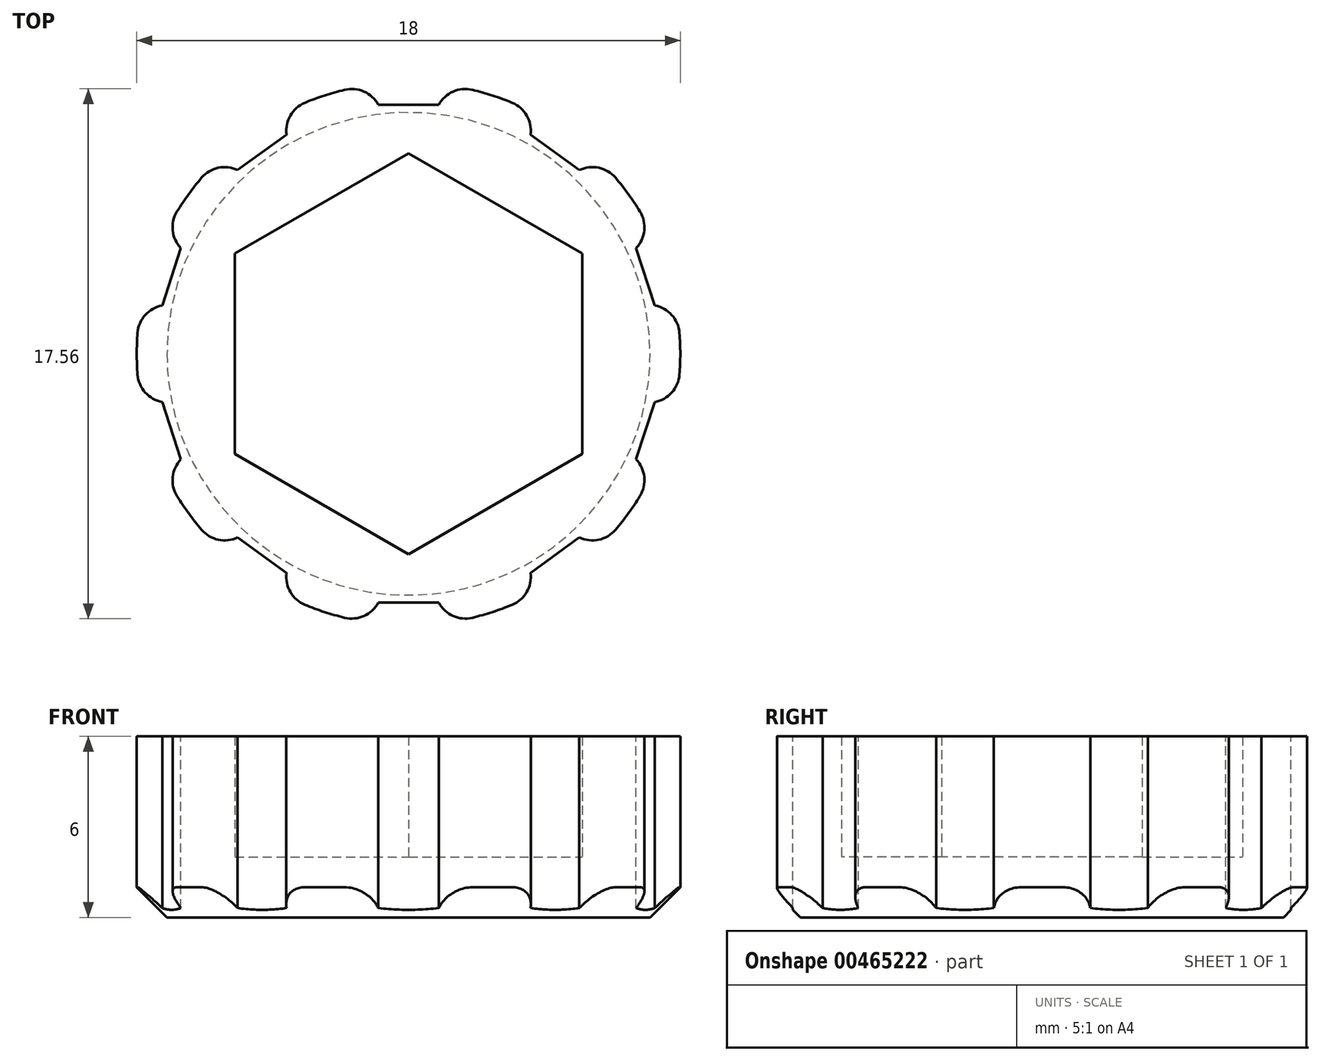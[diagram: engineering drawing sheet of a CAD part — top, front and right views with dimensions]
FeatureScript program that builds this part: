
annotation { "Feature Type Name" : "Feature", "Feature Type Description" : "" }
export const myFeature = defineFeature(function(context is Context, id is Id, definition is map)
    precondition{}
    {
        {
            var Q0;
            Q0=qCreatedBy(makeId("Top.planeOp"),FACE);
            var sketch = newSketch(context, id + "F0", { "sketchPlane" : qUnion([Q0])});
            skCircle(sketch, "E0.cCircle", {"center": v(0, 0) * mm, "radius": 5.75 * mm, "construction": true});
            skLineSegment(sketch, "E0.0", {"start": v(0, 6.64) * mm, "end": v(5.75, 3.32) * mm});
            skLineSegment(sketch, "E0.1", {"start": v(5.75, 3.32) * mm, "end": v(5.75, -3.32) * mm});
            skLineSegment(sketch, "E0.2", {"start": v(5.75, -3.32) * mm, "end": v(0, -6.64) * mm});
            skLineSegment(sketch, "E0.3", {"start": v(0, -6.64) * mm, "end": v(-5.75, -3.32) * mm});
            skLineSegment(sketch, "E0.4", {"start": v(-5.75, -3.32) * mm, "end": v(-5.75, 3.32) * mm});
            skLineSegment(sketch, "E0.5", {"start": v(-5.75, 3.32) * mm, "end": v(0, 6.64) * mm});
            skPoint(sketch, "E0.0.midPoint", {"position": v(2.87, 4.98) * mm});
            skCircle(sketch, "E1", {"center": v(0, 0) * mm, "radius": 9 * mm});
            skSolve(sketch);
        }
        {
            var Q0;
            Q0 = qSketchRegion(id + "F0", true);
            extrude(context, id + "F1", {"entities" : qUnion([Q0]), "depth" : 4 * mm});
        }
        {
            var Q0;
            Q0=makeQuery(id+"F1.opExtrude","CAP_FACE",FACE,{"disambiguationData":[OSD([sQuery(id+"F0.wireOp",EDGE,"E0.0"),sQuery(id+"F0.wireOp",EDGE,"E0.1"),sQuery(id+"F0.wireOp",EDGE,"E0.2"),sQuery(id+"F0.wireOp",EDGE,"E0.3"),sQuery(id+"F0.wireOp",EDGE,"E0.4"),sQuery(id+"F0.wireOp",EDGE,"E0.5"),sQuery(id+"F0.wireOp",EDGE,"E1")])],"isStart":true});
            var sketch = newSketch(context, id + "F2", { "sketchPlane" : qUnion([Q0])});
            skCircle(sketch, "E2.0", {"center": v(0, 0) * mm, "radius": 9 * mm});
            skSolve(sketch);
        }
        {
            var Q0;
            Q0 = qSketchRegion(id + "F2", true);
            extrude(context, id + "F3", {"entities" : qUnion([Q0]), "operationType" : NewBodyOperationType.ADD, "depth" : 2 * mm});
        }
        {
            var Q0;
            Q0=makeQuery(id+"F3.opExtrude","CAP_EDGE",EDGE,{"disambiguationData":[OSD([sQuery(id+"F2.wireOp",EDGE,"E2.0")])],"isStart":false});
            chamfer(context, id + "F4", {"entities" : qUnion([Q0]), "width" : 1 * mm, "tangentPropagation" : true});
        }
        {
            var Q0;
            Q0=makeQuery(id+"F1.opExtrude","CAP_FACE",FACE,{"disambiguationData":[OSD([sQuery(id+"F0.wireOp",EDGE,"E0.0"),sQuery(id+"F0.wireOp",EDGE,"E0.1"),sQuery(id+"F0.wireOp",EDGE,"E0.2"),sQuery(id+"F0.wireOp",EDGE,"E0.3"),sQuery(id+"F0.wireOp",EDGE,"E0.4"),sQuery(id+"F0.wireOp",EDGE,"E0.5"),sQuery(id+"F0.wireOp",EDGE,"E1")])],"isStart":false});
            var sketch = newSketch(context, id + "F5", { "sketchPlane" : qUnion([Q0])});
            skLineSegment(sketch, "E3.bottom", {"start": v(1, 9.75) * mm, "end": v(-1, 9.75) * mm});
            skLineSegment(sketch, "E3.top", {"start": v(1, 8.25) * mm, "end": v(-1, 8.25) * mm});
            skLineSegment(sketch, "E3.left", {"start": v(1, 9.75) * mm, "end": v(1, 8.25) * mm});
            skLineSegment(sketch, "E3.right", {"start": v(-1, 9.75) * mm, "end": v(-1, 8.25) * mm});
            skPoint(sketch, "E3.middle", {"position": v(0, 9) * mm});
            skLineSegment(sketch, "E4.1.0", {"start": v(-4.92, 8.48) * mm, "end": v(-6.54, 7.3) * mm});
            skLineSegment(sketch, "E4.1.1", {"start": v(-6.54, 7.3) * mm, "end": v(-5.66, 6.09) * mm});
            skLineSegment(sketch, "E4.1.2", {"start": v(-4.04, 7.26) * mm, "end": v(-5.66, 6.09) * mm});
            skLineSegment(sketch, "E4.1.3", {"start": v(-4.92, 8.48) * mm, "end": v(-4.04, 7.26) * mm});
            skLineSegment(sketch, "E4.2.0", {"start": v(-8.96, 3.96) * mm, "end": v(-9.58, 2.06) * mm});
            skLineSegment(sketch, "E4.2.1", {"start": v(-9.58, 2.06) * mm, "end": v(-8.16, 1.6) * mm});
            skLineSegment(sketch, "E4.2.2", {"start": v(-7.54, 3.5) * mm, "end": v(-8.16, 1.6) * mm});
            skLineSegment(sketch, "E4.2.3", {"start": v(-8.96, 3.96) * mm, "end": v(-7.54, 3.5) * mm});
            skPoint(sketch, "E4.center", {"position": v(0, 0) * mm});
            skLineSegment(sketch, "E5.2.3.0", {"start": v(-9.58, -2.06) * mm, "end": v(-8.96, -3.96) * mm});
            skLineSegment(sketch, "E5.3.3.0", {"start": v(-8.96, -3.96) * mm, "end": v(-7.54, -3.5) * mm});
            skLineSegment(sketch, "E5.6.3.0", {"start": v(-8.16, -1.6) * mm, "end": v(-7.54, -3.5) * mm});
            skLineSegment(sketch, "E5.9.3.0", {"start": v(-9.58, -2.06) * mm, "end": v(-8.16, -1.6) * mm});
            skLineSegment(sketch, "E5.2.4.0", {"start": v(-6.54, -7.3) * mm, "end": v(-4.92, -8.48) * mm});
            skLineSegment(sketch, "E5.3.4.0", {"start": v(-4.92, -8.48) * mm, "end": v(-4.04, -7.26) * mm});
            skLineSegment(sketch, "E5.6.4.0", {"start": v(-5.66, -6.09) * mm, "end": v(-4.04, -7.26) * mm});
            skLineSegment(sketch, "E5.9.4.0", {"start": v(-6.54, -7.3) * mm, "end": v(-5.66, -6.09) * mm});
            skLineSegment(sketch, "E5.2.5.0", {"start": v(-1, -9.75) * mm, "end": v(1, -9.75) * mm});
            skLineSegment(sketch, "E5.3.5.0", {"start": v(1, -9.75) * mm, "end": v(1, -8.25) * mm});
            skLineSegment(sketch, "E5.6.5.0", {"start": v(-1, -8.25) * mm, "end": v(1, -8.25) * mm});
            skLineSegment(sketch, "E5.9.5.0", {"start": v(-1, -9.75) * mm, "end": v(-1, -8.25) * mm});
            skLineSegment(sketch, "E5.2.6.0", {"start": v(4.92, -8.48) * mm, "end": v(6.54, -7.3) * mm});
            skLineSegment(sketch, "E5.3.6.0", {"start": v(6.54, -7.3) * mm, "end": v(5.66, -6.09) * mm});
            skLineSegment(sketch, "E5.6.6.0", {"start": v(4.04, -7.26) * mm, "end": v(5.66, -6.09) * mm});
            skLineSegment(sketch, "E5.9.6.0", {"start": v(4.92, -8.48) * mm, "end": v(4.04, -7.26) * mm});
            skLineSegment(sketch, "E5.2.7.0", {"start": v(8.96, -3.96) * mm, "end": v(9.58, -2.06) * mm});
            skLineSegment(sketch, "E5.3.7.0", {"start": v(9.58, -2.06) * mm, "end": v(8.16, -1.6) * mm});
            skLineSegment(sketch, "E5.6.7.0", {"start": v(7.54, -3.5) * mm, "end": v(8.16, -1.6) * mm});
            skLineSegment(sketch, "E5.9.7.0", {"start": v(8.96, -3.96) * mm, "end": v(7.54, -3.5) * mm});
            skLineSegment(sketch, "E5.2.8.0", {"start": v(9.58, 2.06) * mm, "end": v(8.96, 3.96) * mm});
            skLineSegment(sketch, "E5.3.8.0", {"start": v(8.96, 3.96) * mm, "end": v(7.54, 3.5) * mm});
            skLineSegment(sketch, "E5.6.8.0", {"start": v(8.16, 1.6) * mm, "end": v(7.54, 3.5) * mm});
            skLineSegment(sketch, "E5.9.8.0", {"start": v(9.58, 2.06) * mm, "end": v(8.16, 1.6) * mm});
            skLineSegment(sketch, "E5.2.9.0", {"start": v(6.54, 7.3) * mm, "end": v(4.92, 8.48) * mm});
            skLineSegment(sketch, "E5.3.9.0", {"start": v(4.92, 8.48) * mm, "end": v(4.04, 7.26) * mm});
            skLineSegment(sketch, "E5.6.9.0", {"start": v(5.66, 6.09) * mm, "end": v(4.04, 7.26) * mm});
            skLineSegment(sketch, "E5.9.9.0", {"start": v(6.54, 7.3) * mm, "end": v(5.66, 6.09) * mm});
            skSolve(sketch);
        }
        {
            var Q0;
            Q0 = qSketchRegion(id + "F5", true);
            extrude(context, id + "F6", {"entities" : qUnion([Q0]), "operationType" : NewBodyOperationType.REMOVE, "endBound" : BoundingType.THROUGH_ALL, "oppositeDirection" : true, "depth" : 25 * mm});
        }
        {
            var Q0;
            Q0=makeQuery(id+"F6.boolean.opBoolean","INTERSECT",EDGE,{"derivedFrom":[makeQuery(id+"F3.boolean.opBoolean","MERGE",FACE,{"derivedFrom":[makeQuery(id+"F1.opExtrude","SWEPT_FACE",FACE,{"disambiguationData":[OSD([sQuery(id+"F0.wireOp",EDGE,"E1")])]}),makeQuery(id+"F3.opExtrude","SWEPT_FACE",FACE,{"disambiguationData":[OSD([sQuery(id+"F2.wireOp",EDGE,"E2.0")])]})]}),makeQuery(id+"F6.opExtrude","SWEPT_FACE",FACE,{"disambiguationData":[OSD([sQuery(id+"F5.wireOp",EDGE,"E3.left")])]})]});
            var Q1;
            Q1=makeQuery(id+"F6.boolean.opBoolean","INTERSECT",EDGE,{"derivedFrom":[makeQuery(id+"F3.boolean.opBoolean","MERGE",FACE,{"derivedFrom":[makeQuery(id+"F1.opExtrude","SWEPT_FACE",FACE,{"disambiguationData":[OSD([sQuery(id+"F0.wireOp",EDGE,"E1")])]}),makeQuery(id+"F3.opExtrude","SWEPT_FACE",FACE,{"disambiguationData":[OSD([sQuery(id+"F2.wireOp",EDGE,"E2.0")])]})]}),makeQuery(id+"F6.opExtrude","SWEPT_FACE",FACE,{"disambiguationData":[OSD([sQuery(id+"F5.wireOp",EDGE,"E5.3.9.0")])]})]});
            var Q2;
            Q2=makeQuery(id+"F6.boolean.opBoolean","INTERSECT",EDGE,{"derivedFrom":[makeQuery(id+"F3.boolean.opBoolean","MERGE",FACE,{"derivedFrom":[makeQuery(id+"F1.opExtrude","SWEPT_FACE",FACE,{"disambiguationData":[OSD([sQuery(id+"F0.wireOp",EDGE,"E1")])]}),makeQuery(id+"F3.opExtrude","SWEPT_FACE",FACE,{"disambiguationData":[OSD([sQuery(id+"F2.wireOp",EDGE,"E2.0")])]})]}),makeQuery(id+"F6.opExtrude","SWEPT_FACE",FACE,{"disambiguationData":[OSD([sQuery(id+"F5.wireOp",EDGE,"E5.9.9.0")])]})]});
            var Q3;
            Q3=makeQuery(id+"F6.boolean.opBoolean","INTERSECT",EDGE,{"derivedFrom":[makeQuery(id+"F3.boolean.opBoolean","MERGE",FACE,{"derivedFrom":[makeQuery(id+"F1.opExtrude","SWEPT_FACE",FACE,{"disambiguationData":[OSD([sQuery(id+"F0.wireOp",EDGE,"E1")])]}),makeQuery(id+"F3.opExtrude","SWEPT_FACE",FACE,{"disambiguationData":[OSD([sQuery(id+"F2.wireOp",EDGE,"E2.0")])]})]}),makeQuery(id+"F6.opExtrude","SWEPT_FACE",FACE,{"disambiguationData":[OSD([sQuery(id+"F5.wireOp",EDGE,"E5.3.8.0")])]})]});
            var Q4;
            Q4=makeQuery(id+"F6.boolean.opBoolean","INTERSECT",EDGE,{"derivedFrom":[makeQuery(id+"F3.boolean.opBoolean","MERGE",FACE,{"derivedFrom":[makeQuery(id+"F1.opExtrude","SWEPT_FACE",FACE,{"disambiguationData":[OSD([sQuery(id+"F0.wireOp",EDGE,"E1")])]}),makeQuery(id+"F3.opExtrude","SWEPT_FACE",FACE,{"disambiguationData":[OSD([sQuery(id+"F2.wireOp",EDGE,"E2.0")])]})]}),makeQuery(id+"F6.opExtrude","SWEPT_FACE",FACE,{"disambiguationData":[OSD([sQuery(id+"F5.wireOp",EDGE,"E5.9.8.0")])]})]});
            var Q5;
            Q5=makeQuery(id+"F6.boolean.opBoolean","INTERSECT",EDGE,{"derivedFrom":[makeQuery(id+"F3.boolean.opBoolean","MERGE",FACE,{"derivedFrom":[makeQuery(id+"F1.opExtrude","SWEPT_FACE",FACE,{"disambiguationData":[OSD([sQuery(id+"F0.wireOp",EDGE,"E1")])]}),makeQuery(id+"F3.opExtrude","SWEPT_FACE",FACE,{"disambiguationData":[OSD([sQuery(id+"F2.wireOp",EDGE,"E2.0")])]})]}),makeQuery(id+"F6.opExtrude","SWEPT_FACE",FACE,{"disambiguationData":[OSD([sQuery(id+"F5.wireOp",EDGE,"E5.3.7.0")])]})]});
            var Q6;
            Q6=makeQuery(id+"F6.boolean.opBoolean","INTERSECT",EDGE,{"derivedFrom":[makeQuery(id+"F3.boolean.opBoolean","MERGE",FACE,{"derivedFrom":[makeQuery(id+"F1.opExtrude","SWEPT_FACE",FACE,{"disambiguationData":[OSD([sQuery(id+"F0.wireOp",EDGE,"E1")])]}),makeQuery(id+"F3.opExtrude","SWEPT_FACE",FACE,{"disambiguationData":[OSD([sQuery(id+"F2.wireOp",EDGE,"E2.0")])]})]}),makeQuery(id+"F6.opExtrude","SWEPT_FACE",FACE,{"disambiguationData":[OSD([sQuery(id+"F5.wireOp",EDGE,"E5.9.7.0")])]})]});
            var Q7;
            Q7=makeQuery(id+"F6.boolean.opBoolean","INTERSECT",EDGE,{"derivedFrom":[makeQuery(id+"F3.boolean.opBoolean","MERGE",FACE,{"derivedFrom":[makeQuery(id+"F1.opExtrude","SWEPT_FACE",FACE,{"disambiguationData":[OSD([sQuery(id+"F0.wireOp",EDGE,"E1")])]}),makeQuery(id+"F3.opExtrude","SWEPT_FACE",FACE,{"disambiguationData":[OSD([sQuery(id+"F2.wireOp",EDGE,"E2.0")])]})]}),makeQuery(id+"F6.opExtrude","SWEPT_FACE",FACE,{"disambiguationData":[OSD([sQuery(id+"F5.wireOp",EDGE,"E5.3.6.0")])]})]});
            var Q8;
            Q8=makeQuery(id+"F6.boolean.opBoolean","INTERSECT",EDGE,{"derivedFrom":[makeQuery(id+"F3.boolean.opBoolean","MERGE",FACE,{"derivedFrom":[makeQuery(id+"F1.opExtrude","SWEPT_FACE",FACE,{"disambiguationData":[OSD([sQuery(id+"F0.wireOp",EDGE,"E1")])]}),makeQuery(id+"F3.opExtrude","SWEPT_FACE",FACE,{"disambiguationData":[OSD([sQuery(id+"F2.wireOp",EDGE,"E2.0")])]})]}),makeQuery(id+"F6.opExtrude","SWEPT_FACE",FACE,{"disambiguationData":[OSD([sQuery(id+"F5.wireOp",EDGE,"E5.9.6.0")])]})]});
            var Q9;
            Q9=makeQuery(id+"F6.boolean.opBoolean","INTERSECT",EDGE,{"derivedFrom":[makeQuery(id+"F3.boolean.opBoolean","MERGE",FACE,{"derivedFrom":[makeQuery(id+"F1.opExtrude","SWEPT_FACE",FACE,{"disambiguationData":[OSD([sQuery(id+"F0.wireOp",EDGE,"E1")])]}),makeQuery(id+"F3.opExtrude","SWEPT_FACE",FACE,{"disambiguationData":[OSD([sQuery(id+"F2.wireOp",EDGE,"E2.0")])]})]}),makeQuery(id+"F6.opExtrude","SWEPT_FACE",FACE,{"disambiguationData":[OSD([sQuery(id+"F5.wireOp",EDGE,"E5.3.5.0")])]})]});
            var Q10;
            Q10=makeQuery(id+"F6.boolean.opBoolean","INTERSECT",EDGE,{"derivedFrom":[makeQuery(id+"F3.boolean.opBoolean","MERGE",FACE,{"derivedFrom":[makeQuery(id+"F1.opExtrude","SWEPT_FACE",FACE,{"disambiguationData":[OSD([sQuery(id+"F0.wireOp",EDGE,"E1")])]}),makeQuery(id+"F3.opExtrude","SWEPT_FACE",FACE,{"disambiguationData":[OSD([sQuery(id+"F2.wireOp",EDGE,"E2.0")])]})]}),makeQuery(id+"F6.opExtrude","SWEPT_FACE",FACE,{"disambiguationData":[OSD([sQuery(id+"F5.wireOp",EDGE,"E5.9.5.0")])]})]});
            var Q11;
            Q11=makeQuery(id+"F6.boolean.opBoolean","INTERSECT",EDGE,{"derivedFrom":[makeQuery(id+"F3.boolean.opBoolean","MERGE",FACE,{"derivedFrom":[makeQuery(id+"F1.opExtrude","SWEPT_FACE",FACE,{"disambiguationData":[OSD([sQuery(id+"F0.wireOp",EDGE,"E1")])]}),makeQuery(id+"F3.opExtrude","SWEPT_FACE",FACE,{"disambiguationData":[OSD([sQuery(id+"F2.wireOp",EDGE,"E2.0")])]})]}),makeQuery(id+"F6.opExtrude","SWEPT_FACE",FACE,{"disambiguationData":[OSD([sQuery(id+"F5.wireOp",EDGE,"E5.3.4.0")])]})]});
            var Q12;
            Q12=makeQuery(id+"F6.boolean.opBoolean","INTERSECT",EDGE,{"derivedFrom":[makeQuery(id+"F3.boolean.opBoolean","MERGE",FACE,{"derivedFrom":[makeQuery(id+"F1.opExtrude","SWEPT_FACE",FACE,{"disambiguationData":[OSD([sQuery(id+"F0.wireOp",EDGE,"E1")])]}),makeQuery(id+"F3.opExtrude","SWEPT_FACE",FACE,{"disambiguationData":[OSD([sQuery(id+"F2.wireOp",EDGE,"E2.0")])]})]}),makeQuery(id+"F6.opExtrude","SWEPT_FACE",FACE,{"disambiguationData":[OSD([sQuery(id+"F5.wireOp",EDGE,"E5.9.4.0")])]})]});
            var Q13;
            Q13=makeQuery(id+"F6.boolean.opBoolean","INTERSECT",EDGE,{"derivedFrom":[makeQuery(id+"F3.boolean.opBoolean","MERGE",FACE,{"derivedFrom":[makeQuery(id+"F1.opExtrude","SWEPT_FACE",FACE,{"disambiguationData":[OSD([sQuery(id+"F0.wireOp",EDGE,"E1")])]}),makeQuery(id+"F3.opExtrude","SWEPT_FACE",FACE,{"disambiguationData":[OSD([sQuery(id+"F2.wireOp",EDGE,"E2.0")])]})]}),makeQuery(id+"F6.opExtrude","SWEPT_FACE",FACE,{"disambiguationData":[OSD([sQuery(id+"F5.wireOp",EDGE,"E5.3.3.0")])]})]});
            var Q14;
            Q14=makeQuery(id+"F6.boolean.opBoolean","INTERSECT",EDGE,{"derivedFrom":[makeQuery(id+"F3.boolean.opBoolean","MERGE",FACE,{"derivedFrom":[makeQuery(id+"F1.opExtrude","SWEPT_FACE",FACE,{"disambiguationData":[OSD([sQuery(id+"F0.wireOp",EDGE,"E1")])]}),makeQuery(id+"F3.opExtrude","SWEPT_FACE",FACE,{"disambiguationData":[OSD([sQuery(id+"F2.wireOp",EDGE,"E2.0")])]})]}),makeQuery(id+"F6.opExtrude","SWEPT_FACE",FACE,{"disambiguationData":[OSD([sQuery(id+"F5.wireOp",EDGE,"E5.9.3.0")])]})]});
            var Q15;
            Q15=makeQuery(id+"F6.boolean.opBoolean","INTERSECT",EDGE,{"derivedFrom":[makeQuery(id+"F3.boolean.opBoolean","MERGE",FACE,{"derivedFrom":[makeQuery(id+"F1.opExtrude","SWEPT_FACE",FACE,{"disambiguationData":[OSD([sQuery(id+"F0.wireOp",EDGE,"E1")])]}),makeQuery(id+"F3.opExtrude","SWEPT_FACE",FACE,{"disambiguationData":[OSD([sQuery(id+"F2.wireOp",EDGE,"E2.0")])]})]}),makeQuery(id+"F6.opExtrude","SWEPT_FACE",FACE,{"disambiguationData":[OSD([sQuery(id+"F5.wireOp",EDGE,"E4.2.1")])]})]});
            var Q16;
            Q16=makeQuery(id+"F6.boolean.opBoolean","INTERSECT",EDGE,{"derivedFrom":[makeQuery(id+"F3.boolean.opBoolean","MERGE",FACE,{"derivedFrom":[makeQuery(id+"F1.opExtrude","SWEPT_FACE",FACE,{"disambiguationData":[OSD([sQuery(id+"F0.wireOp",EDGE,"E1")])]}),makeQuery(id+"F3.opExtrude","SWEPT_FACE",FACE,{"disambiguationData":[OSD([sQuery(id+"F2.wireOp",EDGE,"E2.0")])]})]}),makeQuery(id+"F6.opExtrude","SWEPT_FACE",FACE,{"disambiguationData":[OSD([sQuery(id+"F5.wireOp",EDGE,"E4.2.3")])]})]});
            var Q17;
            Q17=makeQuery(id+"F6.boolean.opBoolean","INTERSECT",EDGE,{"derivedFrom":[makeQuery(id+"F3.boolean.opBoolean","MERGE",FACE,{"derivedFrom":[makeQuery(id+"F1.opExtrude","SWEPT_FACE",FACE,{"disambiguationData":[OSD([sQuery(id+"F0.wireOp",EDGE,"E1")])]}),makeQuery(id+"F3.opExtrude","SWEPT_FACE",FACE,{"disambiguationData":[OSD([sQuery(id+"F2.wireOp",EDGE,"E2.0")])]})]}),makeQuery(id+"F6.opExtrude","SWEPT_FACE",FACE,{"disambiguationData":[OSD([sQuery(id+"F5.wireOp",EDGE,"E4.1.1")])]})]});
            var Q18;
            Q18=makeQuery(id+"F6.boolean.opBoolean","INTERSECT",EDGE,{"derivedFrom":[makeQuery(id+"F3.boolean.opBoolean","MERGE",FACE,{"derivedFrom":[makeQuery(id+"F1.opExtrude","SWEPT_FACE",FACE,{"disambiguationData":[OSD([sQuery(id+"F0.wireOp",EDGE,"E1")])]}),makeQuery(id+"F3.opExtrude","SWEPT_FACE",FACE,{"disambiguationData":[OSD([sQuery(id+"F2.wireOp",EDGE,"E2.0")])]})]}),makeQuery(id+"F6.opExtrude","SWEPT_FACE",FACE,{"disambiguationData":[OSD([sQuery(id+"F5.wireOp",EDGE,"E4.1.3")])]})]});
            var Q19;
            Q19=makeQuery(id+"F6.boolean.opBoolean","INTERSECT",EDGE,{"derivedFrom":[makeQuery(id+"F3.boolean.opBoolean","MERGE",FACE,{"derivedFrom":[makeQuery(id+"F1.opExtrude","SWEPT_FACE",FACE,{"disambiguationData":[OSD([sQuery(id+"F0.wireOp",EDGE,"E1")])]}),makeQuery(id+"F3.opExtrude","SWEPT_FACE",FACE,{"disambiguationData":[OSD([sQuery(id+"F2.wireOp",EDGE,"E2.0")])]})]}),makeQuery(id+"F6.opExtrude","SWEPT_FACE",FACE,{"disambiguationData":[OSD([sQuery(id+"F5.wireOp",EDGE,"E3.right")])]})]});
            fillet(context, id + "F7", {"entities" : qUnion([Q0, Q1, Q2, Q3, Q4, Q5, Q6, Q7, Q8, Q9, Q10, Q11, Q12, Q13, Q14, Q15, Q16, Q17, Q18, Q19]), "radius" : 1 * mm, "tangentPropagation" : true, "allowEdgeOverflow" : false});
        }
    });
